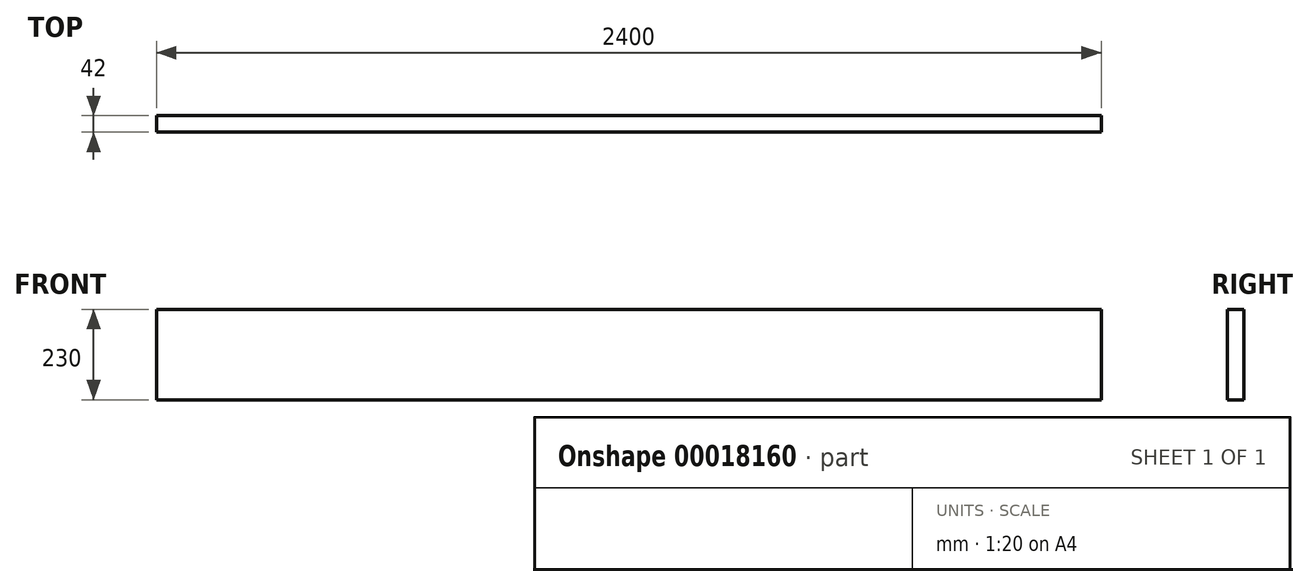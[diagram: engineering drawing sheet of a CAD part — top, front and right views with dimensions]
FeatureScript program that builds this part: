
annotation { "Feature Type Name" : "Feature", "Feature Type Description" : "" }
export const myFeature = defineFeature(function(context is Context, id is Id, definition is map)
    precondition{}
    {
        {
            var Q0;
            Q0=qCreatedBy(makeId("Right.planeOp"),FACE);
            var sketch = newSketch(context, id + "F0", { "sketchPlane" : qUnion([Q0])});
            skLineSegment(sketch, "E0.rect.bottom", {"start": v(-21, 115) * mm, "end": v(21, 115) * mm});
            skLineSegment(sketch, "E0.rect.top", {"start": v(-21, -115) * mm, "end": v(21, -115) * mm});
            skLineSegment(sketch, "E0.rect.left", {"start": v(-21, 115) * mm, "end": v(-21, -115) * mm});
            skLineSegment(sketch, "E0.rect.right", {"start": v(21, 115) * mm, "end": v(21, -115) * mm});
            skPoint(sketch, "E0.rect.middle", {"position": v(0, 0) * mm});
            skSolve(sketch);
        }
        {
            var Q0;
            Q0=qSketchRegion(id+"F0",true);
            extrude(context, id + "F1", {"entities" : qUnion([Q0]), "endBound" : BoundingType.SYMMETRIC, "depth" : 2400 * mm});
        }
    });
